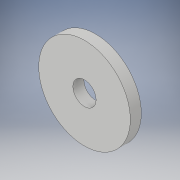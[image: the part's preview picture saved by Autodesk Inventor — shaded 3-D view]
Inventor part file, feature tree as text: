
AUTODESK INVENTOR PART (.ipt)
format: ipt  version: 2019 (Build 230136000, 136)  size: 99,840 bytes
history: native  units: in
note: dims shown in document units (in); Inventor stores cm internally (conversion verified against a paired STEP export)
features: extrude x1, sketch x1
ambient origin geometry x8: Origin, YZ Plane, XZ Plane, XY Plane, X Axis, Y Axis, Z Axis, Center Point
bodies: Solid1 (feature_tree)
feature tree (2):
  extrude  "Extrusion1"  Depth=0.09in
  sketch  "Sketch1"  dims[d0=0.19in d1=0.75in d2=0.09in d3=0.0in]
